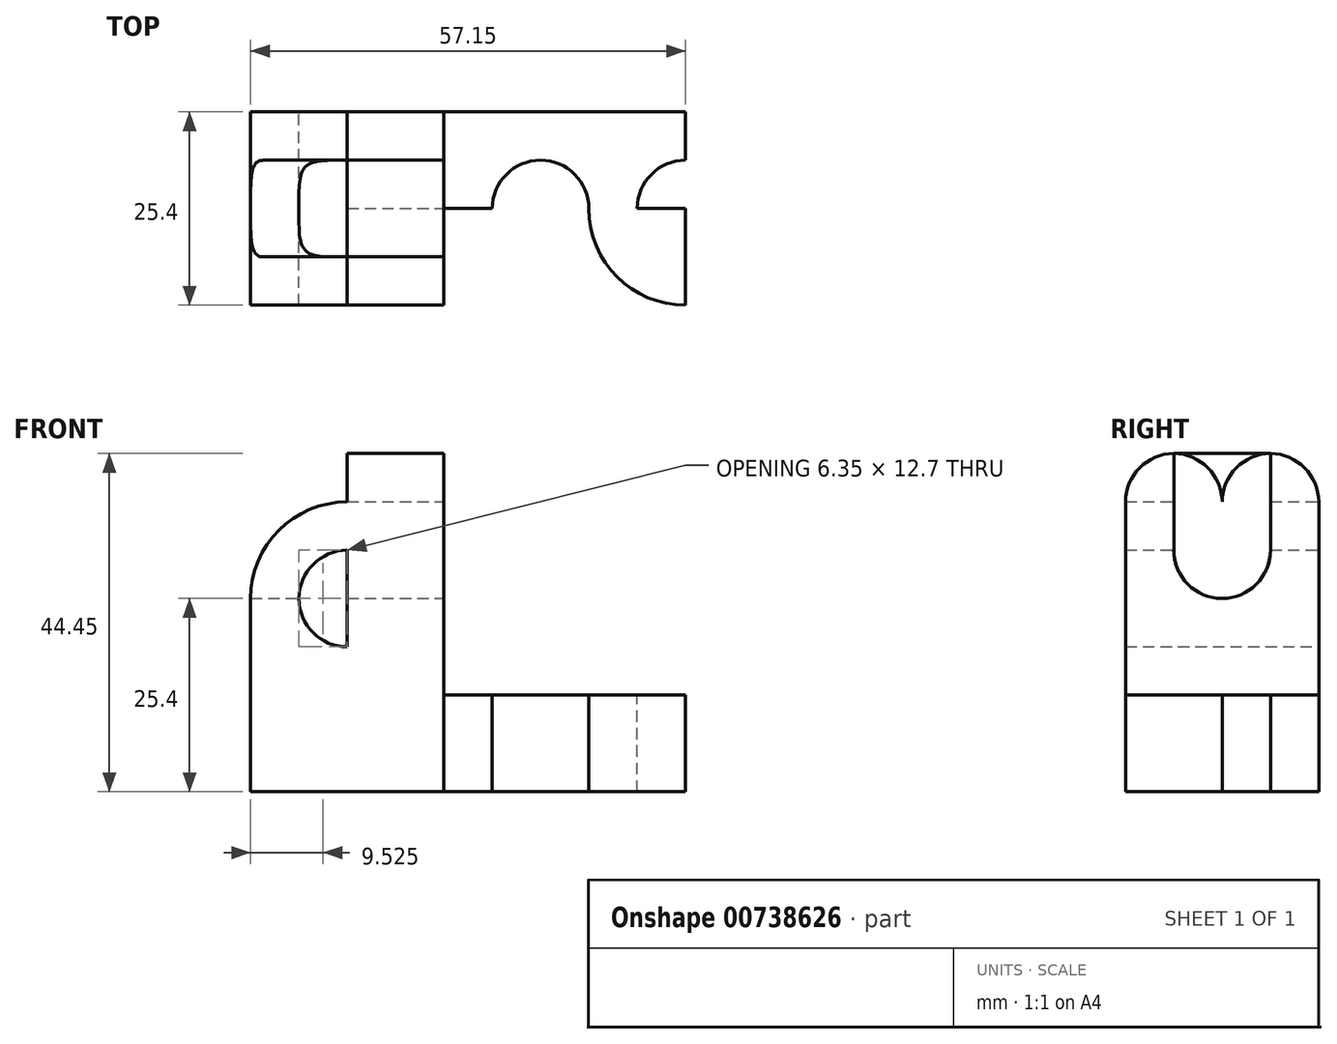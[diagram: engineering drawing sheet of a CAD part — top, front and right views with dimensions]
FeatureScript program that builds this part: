
annotation { "Feature Type Name" : "Feature", "Feature Type Description" : "" }
export const myFeature = defineFeature(function(context is Context, id is Id, definition is map)
    precondition{}
    {
        {
            var Q0;
            Q0=qCreatedBy(makeId("Front.planeOp"),FACE);
            var sketch = newSketch(context, id + "F0", { "sketchPlane" : qUnion([Q0])});
            skLineSegment(sketch, "E0", {"start": v(0, 25.4) * mm, "end": v(0, 0) * mm});
            skLineSegment(sketch, "E1", {"start": v(0, 0) * mm, "end": v(57.15, 0) * mm});
            skLineSegment(sketch, "E2", {"start": v(57.15, 0) * mm, "end": v(57.15, 12.7) * mm});
            skLineSegment(sketch, "E3", {"start": v(57.15, 0) * mm, "end": v(69.85, 0) * mm});
            skLineSegment(sketch, "E4", {"start": v(57.15, 12.7) * mm, "end": v(25.4, 12.7) * mm});
            skLineSegment(sketch, "E5", {"start": v(25.4, 12.7) * mm, "end": v(25.4, 25.4) * mm});
            skLineSegment(sketch, "E6", {"start": v(0, 25.4) * mm, "end": v(25.4, 25.4) * mm});
            skCircle(sketch, "E7", {"center": v(12.7, 25.4) * mm, "radius": 6.35 * mm});
            skCircle(sketch, "E8", {"center": v(12.7, 25.4) * mm, "radius": 12.7 * mm});
            skLineSegment(sketch, "E9.bottom", {"start": v(69.85, 0) * mm, "end": v(57.15, 0) * mm});
            skLineSegment(sketch, "E9.top", {"start": v(69.85, 12.7) * mm, "end": v(57.15, 12.7) * mm});
            skLineSegment(sketch, "E9.left", {"start": v(69.85, 0) * mm, "end": v(69.85, 12.7) * mm});
            skSolve(sketch);
        }
        {
            var Q0;
            Q0=makeQuery(id+"F0.imprint","IMPRINT",FACE,{"disambiguationData":[TD([[makeQuery(id+"F0.imprint","IMPRINT",EDGE,{"derivedFrom":sQuery(id+"F0.wireOp",EDGE,"E9.bottom")}),-1.0]])]});
            var Q1;
            {var subQ1=sQuery(id+"F0.wireOp",EDGE,"E0");Q1=makeQuery(id+"F0.imprint","IMPRINT",FACE,{"disambiguationData":[TD([[makeQuery(id+"F0.imprint","IMPRINT",EDGE,{"derivedFrom":subQ1}),1.0]])]});}
            var Q2;
            {var subQ1=sQuery(id+"F0.wireOp",EDGE,"E6");var subQ3=sQuery(id+"F0.wireOp",EDGE,"E7");var subQ4=makeQuery(id+"F0.imprint","INTERSECT",VERTEX,{"disambiguationData":[OD(0.0)],"derivedFrom":[subQ1,subQ3]});Q2=makeQuery(id+"F0.imprint","IMPRINT",FACE,{"disambiguationData":[TD([[makeQuery(id+"F0.imprint","IMPRINT",EDGE,{"disambiguationData":[TD([[subQ4,-1.0]])],"derivedFrom":subQ3}),-1.0]])]});}
            var Q3;
            {var subQ1=sQuery(id+"F0.wireOp",EDGE,"E6");var subQ3=sQuery(id+"F0.wireOp",EDGE,"E7");var subQ4=makeQuery(id+"F0.imprint","INTERSECT",VERTEX,{"disambiguationData":[OD(0.0)],"derivedFrom":[subQ1,subQ3]});Q3=makeQuery(id+"F0.imprint","IMPRINT",FACE,{"disambiguationData":[TD([[makeQuery(id+"F0.imprint","IMPRINT",EDGE,{"disambiguationData":[TD([[subQ4,1.0]])],"derivedFrom":subQ3}),-1.0]])]});}
            extrude(context, id + "F1", {"entities" : qUnion([Q0, Q1, Q2, Q3]), "depth" : 25.4 * mm, "offsetDistance" : 25.4 * mm});
        }
        {
            var Q0;
            Q0=makeQuery(id+"F1.opExtrude","SWEPT_FACE",FACE,{"disambiguationData":[OSD([sQuery(id+"F0.wireOp",EDGE,"E4"),sQuery(id+"F0.wireOp",EDGE,"E9.top")])]});
            var sketch = newSketch(context, id + "F2", { "sketchPlane" : qUnion([Q0])});
            skLineSegment(sketch, "E10", {"start": v(25.4, -12.7) * mm, "end": v(57.15, -12.7) * mm});
            skCircle(sketch, "E11", {"center": v(57.15, -12.7) * mm, "radius": 6.35 * mm});
            skCircle(sketch, "E12", {"center": v(57.15, -12.7) * mm, "radius": 12.7 * mm});
            skSolve(sketch);
        }
        {
            var Q0;
            {var subQ0=sQuery(id+"F2.wireOp",EDGE,"E12");var subQ1=sQuery(id+"F0.wireOp",EDGE,"E9.top");var subQ2=makeQuery(id+"F1.opExtrude","CAP_EDGE",EDGE,{"disambiguationData":[OSD([sQuery(id+"F0.wireOp",EDGE,"E4"),subQ1])],"isStart":true});var subQ3=makeQuery(id+"F2.imprint","INTERSECT",VERTEX,{"derivedFrom":[subQ2,subQ0]});Q0=makeQuery(id+"F2.imprint","IMPRINT",FACE,{"disambiguationData":[TD([[makeQuery(id+"F2.imprint","IMPRINT",EDGE,{"disambiguationData":[TD([[subQ3,1.0]])],"derivedFrom":subQ0}),-1.0]])]});}
            var Q1;
            {var subQ0=sQuery(id+"F2.wireOp",EDGE,"E12");var subQ1=sQuery(id+"F0.wireOp",EDGE,"E9.top");var subQ2=makeQuery(id+"F1.opExtrude","SWEPT_EDGE",EDGE,{"disambiguationData":[OSD([subQ1,sQuery(id+"F0.wireOp",EDGE,"E9.left")])]});var subQ3=makeQuery(id+"F2.imprint","INTERSECT",VERTEX,{"derivedFrom":[subQ2,subQ0]});Q1=makeQuery(id+"F2.imprint","IMPRINT",FACE,{"disambiguationData":[TD([[makeQuery(id+"F2.imprint","IMPRINT",EDGE,{"disambiguationData":[TD([[subQ3,1.0]])],"derivedFrom":subQ0}),-1.0]])]});}
            extrude(context, id + "F3", {"entities" : qUnion([Q0, Q1]), "operationType" : NewBodyOperationType.REMOVE, "endBound" : BoundingType.THROUGH_ALL, "oppositeDirection" : true, "depth" : 25.4 * mm, "offsetDistance" : 25.4 * mm});
        }
        {
            var Q0;
            Q0=makeQuery(id+"F1.opExtrude","SWEPT_FACE",FACE,{"disambiguationData":[OSD([sQuery(id+"F0.wireOp",EDGE,"E4"),sQuery(id+"F0.wireOp",EDGE,"E9.top")])]});
            var sketch = newSketch(context, id + "F4", { "sketchPlane" : qUnion([Q0])});
            skLineSegment(sketch, "E13", {"start": v(25.4, -12.7) * mm, "end": v(57.15, -12.7) * mm});
            skCircle(sketch, "E14", {"center": v(57.15, -12.7) * mm, "radius": 6.35 * mm});
            skLineSegment(sketch, "E15", {"start": v(25.4, -12.7) * mm, "end": v(38.1, -12.7) * mm});
            skCircle(sketch, "E16", {"center": v(38.1, -12.7) * mm, "radius": 6.35 * mm});
            skLineSegment(sketch, "E17", {"start": v(57.15, -12.7) * mm, "end": v(57.15, -6.35) * mm});
            skLineSegment(sketch, "E18", {"start": v(57.15, -12.7) * mm, "end": v(57.15, -19.05) * mm});
            skLineSegment(sketch, "E19", {"start": v(38.1, -12.7) * mm, "end": v(38.1, -19.05) * mm});
            skLineSegment(sketch, "E20", {"start": v(38.1, -12.7) * mm, "end": v(38.1, -6.35) * mm});
            skLineSegment(sketch, "E21", {"start": v(38.1, -6.35) * mm, "end": v(57.15, -6.35) * mm});
            skLineSegment(sketch, "E22", {"start": v(38.1, -19.05) * mm, "end": v(57.15, -19.05) * mm});
            skSolve(sketch);
        }
        {
            var Q0;
            {var subQ0=sQuery(id+"F4.wireOp",EDGE,"E20");Q0=makeQuery(id+"F4.imprint","IMPRINT",FACE,{"disambiguationData":[TD([[makeQuery(id+"F4.imprint","IMPRINT",EDGE,{"derivedFrom":subQ0}),1.0]])]});}
            var Q1;
            {var subQ0=sQuery(id+"F4.wireOp",EDGE,"E20");Q1=makeQuery(id+"F4.imprint","IMPRINT",FACE,{"disambiguationData":[TD([[makeQuery(id+"F4.imprint","IMPRINT",EDGE,{"derivedFrom":subQ0}),-1.0]])]});}
            var Q2;
            {var subQ0=sQuery(id+"F4.wireOp",EDGE,"E19");Q2=makeQuery(id+"F4.imprint","IMPRINT",FACE,{"disambiguationData":[TD([[makeQuery(id+"F4.imprint","IMPRINT",EDGE,{"derivedFrom":subQ0}),1.0]])]});}
            var Q3;
            {var subQ0=sQuery(id+"F4.wireOp",EDGE,"E19");Q3=makeQuery(id+"F4.imprint","IMPRINT",FACE,{"disambiguationData":[TD([[makeQuery(id+"F4.imprint","IMPRINT",EDGE,{"derivedFrom":subQ0}),-1.0]])]});}
            var Q4;
            {var subQ0=sQuery(id+"F4.wireOp",EDGE,"E18");Q4=makeQuery(id+"F4.imprint","IMPRINT",FACE,{"disambiguationData":[TD([[makeQuery(id+"F4.imprint","IMPRINT",EDGE,{"derivedFrom":subQ0}),-1.0]])]});}
            var Q5;
            {var subQ0=sQuery(id+"F4.wireOp",EDGE,"E17");Q5=makeQuery(id+"F4.imprint","IMPRINT",FACE,{"disambiguationData":[TD([[makeQuery(id+"F4.imprint","IMPRINT",EDGE,{"derivedFrom":subQ0}),1.0]])]});}
            var Q6;
            {var subQ0=sQuery(id+"F4.wireOp",EDGE,"E17");Q6=makeQuery(id+"F4.imprint","IMPRINT",FACE,{"disambiguationData":[TD([[makeQuery(id+"F4.imprint","IMPRINT",EDGE,{"derivedFrom":subQ0}),-1.0]])]});}
            extrude(context, id + "F5", {"entities" : qUnion([Q0, Q1, Q2, Q3, Q4, Q5, Q6]), "operationType" : NewBodyOperationType.REMOVE, "endBound" : BoundingType.THROUGH_ALL, "oppositeDirection" : true, "depth" : 25.4 * mm, "offsetDistance" : 25.4 * mm});
        }
        {
            var Q0;
            Q0=makeQuery(id+"F1.opExtrude","CAP_FACE",FACE,{"disambiguationData":[OSD([sQuery(id+"F0.wireOp",EDGE,"E0"),sQuery(id+"F0.wireOp",EDGE,"E1"),sQuery(id+"F0.wireOp",EDGE,"E4"),sQuery(id+"F0.wireOp",EDGE,"E5"),sQuery(id+"F0.wireOp",EDGE,"E7"),sQuery(id+"F0.wireOp",EDGE,"E8"),sQuery(id+"F0.wireOp",EDGE,"E9.bottom"),sQuery(id+"F0.wireOp",EDGE,"E9.top"),sQuery(id+"F0.wireOp",EDGE,"E9.left")])],"isStart":false});
            var sketch = newSketch(context, id + "F6", { "sketchPlane" : qUnion([Q0])});
            skLineSegment(sketch, "E23.bottom", {"start": v(25.4, 12.7) * mm, "end": v(12.7, 12.7) * mm});
            skLineSegment(sketch, "E23.top", {"start": v(25.4, 44.45) * mm, "end": v(12.7, 44.45) * mm});
            skLineSegment(sketch, "E23.left", {"start": v(25.4, 12.7) * mm, "end": v(25.4, 44.45) * mm});
            skLineSegment(sketch, "E23.right", {"start": v(12.7, 12.7) * mm, "end": v(12.7, 44.45) * mm});
            skSolve(sketch);
        }
        {
            var Q0;
            {var subQ0=sQuery(id+"F6.wireOp",EDGE,"E23.right");var subQ1=makeQuery(id+"F1.opExtrude","CAP_EDGE",EDGE,{"disambiguationData":[OSD([sQuery(id+"F0.wireOp",EDGE,"E7")])],"isStart":false});var subQ2=makeQuery(id+"F6.imprint","INTERSECT",VERTEX,{"disambiguationData":[OD(0.0)],"derivedFrom":[subQ1,subQ0]});Q0=makeQuery(id+"F6.imprint","IMPRINT",FACE,{"disambiguationData":[TD([[makeQuery(id+"F6.imprint","IMPRINT",EDGE,{"disambiguationData":[TD([[subQ2,-1.0]])],"derivedFrom":subQ0}),-1.0]])]});}
            var Q1;
            {var subQ5=sQuery(id+"F6.wireOp",EDGE,"E23.bottom");Q1=makeQuery(id+"F6.imprint","IMPRINT",FACE,{"disambiguationData":[TD([[makeQuery(id+"F6.imprint","IMPRINT",EDGE,{"derivedFrom":subQ5}),-1.0]])]});}
            var Q2;
            {var subQ0=sQuery(id+"F6.wireOp",EDGE,"E23.top");Q2=makeQuery(id+"F6.imprint","IMPRINT",FACE,{"disambiguationData":[TD([[makeQuery(id+"F6.imprint","IMPRINT",EDGE,{"derivedFrom":subQ0}),1.0]])]});}
            extrude(context, id + "F7", {"entities" : qUnion([Q0, Q1, Q2]), "operationType" : NewBodyOperationType.ADD, "oppositeDirection" : true, "depth" : 25.4 * mm, "offsetDistance" : 25.4 * mm});
        }
        {
            var Q0;
            Q0=makeQuery(id+"F7.boolean.opBoolean","MERGE",FACE,{"derivedFrom":[makeQuery(id+"F1.opExtrude","CAP_FACE",FACE,{"disambiguationData":[OSD([sQuery(id+"F0.wireOp",EDGE,"E0"),sQuery(id+"F0.wireOp",EDGE,"E1"),sQuery(id+"F0.wireOp",EDGE,"E4"),sQuery(id+"F0.wireOp",EDGE,"E5"),sQuery(id+"F0.wireOp",EDGE,"E7"),sQuery(id+"F0.wireOp",EDGE,"E8"),sQuery(id+"F0.wireOp",EDGE,"E9.bottom"),sQuery(id+"F0.wireOp",EDGE,"E9.top"),sQuery(id+"F0.wireOp",EDGE,"E9.left")])],"isStart":false}),makeQuery(id+"F7.opExtrude","CAP_FACE",FACE,{"disambiguationData":[OSD([sQuery(id+"F6.wireOp",EDGE,"E23.bottom"),sQuery(id+"F6.wireOp",EDGE,"E23.top"),sQuery(id+"F6.wireOp",EDGE,"E23.left"),sQuery(id+"F6.wireOp",EDGE,"E23.right")])],"isStart":true})]});
            var sketch = newSketch(context, id + "F8", { "sketchPlane" : qUnion([Q0])});
            skLineSegment(sketch, "E24.bottom", {"start": v(0, 0) * mm, "end": v(12.7, 0) * mm});
            skLineSegment(sketch, "E24.top", {"start": v(0, 44.45) * mm, "end": v(12.7, 44.45) * mm});
            skLineSegment(sketch, "E24.left", {"start": v(0, 0) * mm, "end": v(0, 44.45) * mm});
            skLineSegment(sketch, "E24.right", {"start": v(12.7, 0) * mm, "end": v(12.7, 44.45) * mm});
            skSolve(sketch);
        }
        {
            var Q0;
            {var subQ0=sQuery(id+"F8.wireOp",EDGE,"E24.top");Q0=makeQuery(id+"F8.imprint","IMPRINT",FACE,{"disambiguationData":[TD([[makeQuery(id+"F8.imprint","IMPRINT",EDGE,{"derivedFrom":subQ0}),-1.0]])]});}
            var Q1;
            {var subQ3=sQuery(id+"F8.wireOp",EDGE,"E24.bottom");Q1=makeQuery(id+"F8.imprint","IMPRINT",FACE,{"disambiguationData":[TD([[makeQuery(id+"F8.imprint","IMPRINT",EDGE,{"derivedFrom":subQ3}),-1.0]])]});}
            var Q2;
            {var subQ1=makeQuery(id+"F1.opExtrude","CAP_EDGE",EDGE,{"disambiguationData":[OSD([sQuery(id+"F0.wireOp",EDGE,"E7")])],"isStart":false});Q2=makeQuery(id+"F8.imprint","IMPRINT",FACE,{"disambiguationData":[TD([[makeQuery(id+"F8.imprint","IMPRINT",EDGE,{"derivedFrom":subQ1}),1.0]])]});}
            extrude(context, id + "F9", {"entities" : qUnion([Q0, Q1, Q2]), "operationType" : NewBodyOperationType.REMOVE, "endBound" : BoundingType.THROUGH_ALL, "oppositeDirection" : true, "depth" : 25.4 * mm, "offsetDistance" : 25.4 * mm});
        }
        {
            var Q0;
            Q0=makeQuery(id+"F7.boolean.opBoolean","MERGE",FACE,{"derivedFrom":[makeQuery(id+"F1.opExtrude","SWEPT_FACE",FACE,{"disambiguationData":[OSD([sQuery(id+"F0.wireOp",EDGE,"E5")])]}),makeQuery(id+"F7.opExtrude","SWEPT_FACE",FACE,{"disambiguationData":[OSD([sQuery(id+"F6.wireOp",EDGE,"E23.left")])]})]});
            var sketch = newSketch(context, id + "F10", { "sketchPlane" : qUnion([Q0])});
            skLineSegment(sketch, "E25", {"start": v(-12.7, 44.45) * mm, "end": v(-12.7, 31.75) * mm});
            skCircle(sketch, "E26", {"center": v(-12.7, 31.75) * mm, "radius": 6.35 * mm});
            skLineSegment(sketch, "E27", {"start": v(-12.7, 44.45) * mm, "end": v(-12.7, 38.1) * mm});
            skLineSegment(sketch, "E28", {"start": v(-12.7, 38.1) * mm, "end": v(-25.4, 38.1) * mm});
            skLineSegment(sketch, "E29", {"start": v(-12.7, 38.1) * mm, "end": v(0, 38.1) * mm});
            skCircle(sketch, "E30", {"center": v(-19.05, 38.1) * mm, "radius": 6.35 * mm});
            skCircle(sketch, "E31", {"center": v(-6.35, 38.1) * mm, "radius": 6.35 * mm});
            skLineSegment(sketch, "E32", {"start": v(-19.05, 38.1) * mm, "end": v(-19.05, 31.75) * mm});
            skLineSegment(sketch, "E33", {"start": v(-19.05, 38.1) * mm, "end": v(-19.05, 44.45) * mm});
            skLineSegment(sketch, "E34", {"start": v(-6.35, 38.1) * mm, "end": v(-6.35, 44.45) * mm});
            skLineSegment(sketch, "E35", {"start": v(-6.35, 38.1) * mm, "end": v(-6.35, 31.75) * mm});
            skSolve(sketch);
        }
        {
            var Q0;
            {var subQ0=sQuery(id+"F10.wireOp",EDGE,"E30");var subQ1=sQuery(id+"F6.wireOp",EDGE,"E23.left");var subQ2=makeQuery(id+"F7.boolean.opBoolean","MERGE",EDGE,{"derivedFrom":[makeQuery(id+"F1.opExtrude","CAP_EDGE",EDGE,{"disambiguationData":[OSD([sQuery(id+"F0.wireOp",EDGE,"E5")])],"isStart":false}),makeQuery(id+"F7.opExtrude","CAP_EDGE",EDGE,{"disambiguationData":[OSD([subQ1])],"isStart":true})]});var subQ3=makeQuery(id+"F10.imprint","INTERSECT",VERTEX,{"derivedFrom":[subQ2,sQuery(id+"F10.wireOp",EDGE,"E28"),subQ0]});Q0=makeQuery(id+"F10.imprint","IMPRINT",FACE,{"disambiguationData":[TD([[makeQuery(id+"F10.imprint","IMPRINT",EDGE,{"disambiguationData":[TD([[subQ3,1.0]])],"derivedFrom":subQ0}),-1.0]])]});}
            var Q1;
            {var subQ0=sQuery(id+"F10.wireOp",EDGE,"E31");var subQ1=sQuery(id+"F6.wireOp",EDGE,"E23.left");var subQ2=makeQuery(id+"F7.boolean.opBoolean","MERGE",EDGE,{"derivedFrom":[makeQuery(id+"F1.opExtrude","CAP_EDGE",EDGE,{"disambiguationData":[OSD([sQuery(id+"F0.wireOp",EDGE,"E5")])],"isStart":true}),makeQuery(id+"F7.opExtrude","CAP_EDGE",EDGE,{"disambiguationData":[OSD([subQ1])],"isStart":false})]});var subQ3=makeQuery(id+"F10.imprint","INTERSECT",VERTEX,{"derivedFrom":[subQ2,sQuery(id+"F10.wireOp",EDGE,"E29"),subQ0]});Q1=makeQuery(id+"F10.imprint","IMPRINT",FACE,{"disambiguationData":[TD([[makeQuery(id+"F10.imprint","IMPRINT",EDGE,{"disambiguationData":[TD([[subQ3,-1.0]])],"derivedFrom":subQ0}),-1.0]])]});}
            var Q2;
            {var subQ3=sQuery(id+"F10.wireOp",EDGE,"E34");Q2=makeQuery(id+"F10.imprint","IMPRINT",FACE,{"disambiguationData":[TD([[makeQuery(id+"F10.imprint","IMPRINT",EDGE,{"derivedFrom":subQ3}),1.0]])]});}
            var Q3;
            {var subQ0=sQuery(id+"F10.wireOp",EDGE,"E27");Q3=makeQuery(id+"F10.imprint","IMPRINT",FACE,{"disambiguationData":[TD([[makeQuery(id+"F10.imprint","IMPRINT",EDGE,{"derivedFrom":subQ0}),1.0]])]});}
            var Q4;
            {var subQ0=sQuery(id+"F10.wireOp",EDGE,"E27");Q4=makeQuery(id+"F10.imprint","IMPRINT",FACE,{"disambiguationData":[TD([[makeQuery(id+"F10.imprint","IMPRINT",EDGE,{"derivedFrom":subQ0}),-1.0]])]});}
            var Q5;
            {var subQ3=sQuery(id+"F10.wireOp",EDGE,"E33");Q5=makeQuery(id+"F10.imprint","IMPRINT",FACE,{"disambiguationData":[TD([[makeQuery(id+"F10.imprint","IMPRINT",EDGE,{"derivedFrom":subQ3}),-1.0]])]});}
            var Q6;
            {var subQ4=sQuery(id+"F10.wireOp",EDGE,"E32");Q6=makeQuery(id+"F10.imprint","IMPRINT",FACE,{"disambiguationData":[TD([[makeQuery(id+"F10.imprint","IMPRINT",EDGE,{"derivedFrom":subQ4}),1.0]])]});}
            var Q7;
            {var subQ0=sQuery(id+"F10.wireOp",EDGE,"E30");var subQ1=sQuery(id+"F10.wireOp",EDGE,"E26");var subQ3=makeQuery(id+"F10.imprint","INTERSECT",VERTEX,{"derivedFrom":[subQ1,subQ0,sQuery(id+"F10.wireOp",EDGE,"E32")]});Q7=makeQuery(id+"F10.imprint","IMPRINT",FACE,{"disambiguationData":[TD([[makeQuery(id+"F10.imprint","IMPRINT",EDGE,{"disambiguationData":[TD([[subQ3,1.0]])],"derivedFrom":subQ1}),1.0]])]});}
            var Q8;
            {var subQ0=sQuery(id+"F10.wireOp",EDGE,"E31");var subQ1=sQuery(id+"F10.wireOp",EDGE,"E26");var subQ3=makeQuery(id+"F10.imprint","INTERSECT",VERTEX,{"derivedFrom":[subQ1,subQ0,sQuery(id+"F10.wireOp",EDGE,"E35")]});Q8=makeQuery(id+"F10.imprint","IMPRINT",FACE,{"disambiguationData":[TD([[makeQuery(id+"F10.imprint","IMPRINT",EDGE,{"disambiguationData":[TD([[subQ3,-1.0]])],"derivedFrom":subQ1}),1.0]])]});}
            var Q9;
            {var subQ0=sQuery(id+"F10.wireOp",EDGE,"E30");var subQ1=sQuery(id+"F10.wireOp",EDGE,"E26");var subQ2=makeQuery(id+"F10.imprint","INTERSECT",VERTEX,{"derivedFrom":[subQ1,subQ0,sQuery(id+"F10.wireOp",EDGE,"E32")]});Q9=makeQuery(id+"F10.imprint","IMPRINT",FACE,{"disambiguationData":[TD([[makeQuery(id+"F10.imprint","IMPRINT",EDGE,{"disambiguationData":[TD([[subQ2,-1.0]])],"derivedFrom":subQ1}),1.0]])]});}
            var Q10;
            {var subQ4=sQuery(id+"F10.wireOp",EDGE,"E35");Q10=makeQuery(id+"F10.imprint","IMPRINT",FACE,{"disambiguationData":[TD([[makeQuery(id+"F10.imprint","IMPRINT",EDGE,{"derivedFrom":subQ4}),-1.0]])]});}
            extrude(context, id + "F11", {"entities" : qUnion([Q0, Q1, Q2, Q3, Q4, Q5, Q6, Q7, Q8, Q9, Q10]), "operationType" : NewBodyOperationType.REMOVE, "endBound" : BoundingType.THROUGH_ALL, "oppositeDirection" : true, "depth" : 25.4 * mm, "offsetDistance" : 25.4 * mm});
        }
    });
